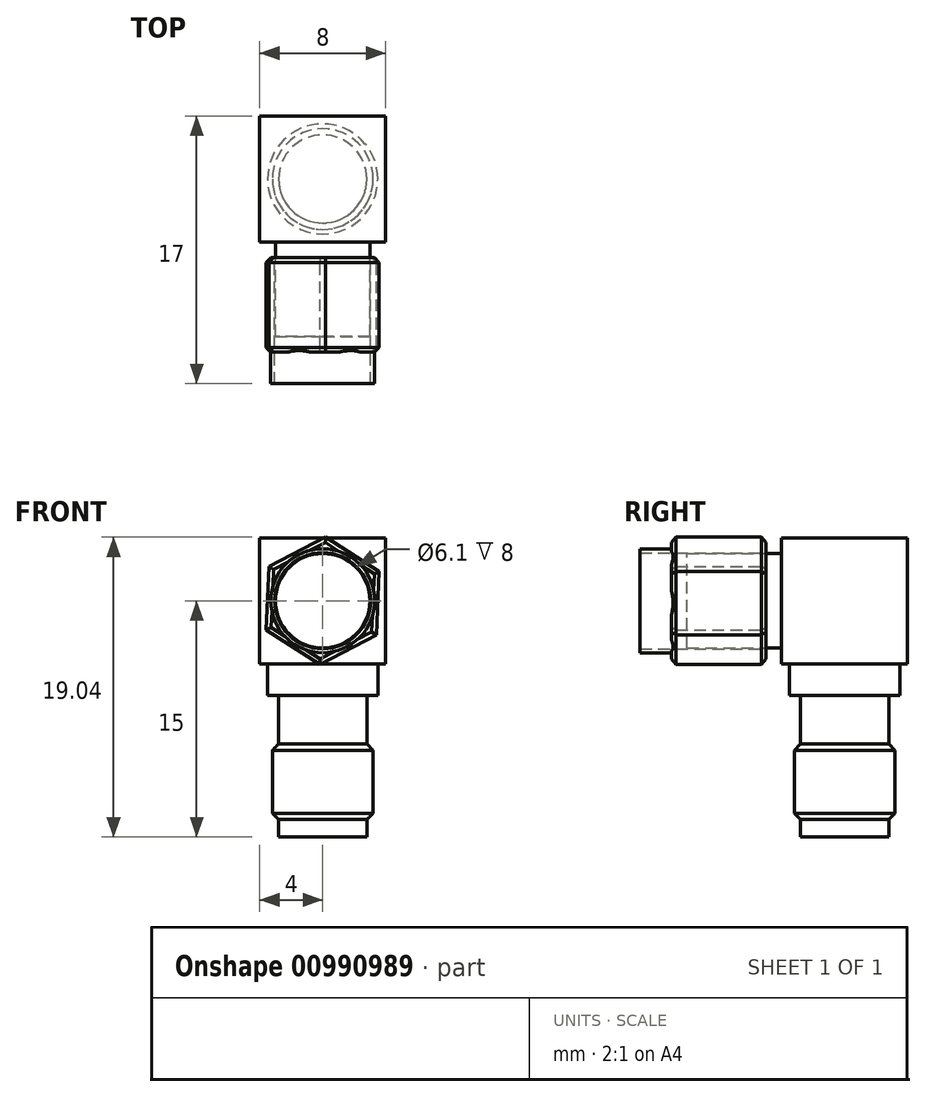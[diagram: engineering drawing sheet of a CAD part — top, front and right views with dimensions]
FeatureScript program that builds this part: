
annotation { "Feature Type Name" : "Feature", "Feature Type Description" : "" }
export const myFeature = defineFeature(function(context is Context, id is Id, definition is map)
    precondition{}
    {
        {
            var Q0;
            Q0=qCreatedBy(makeId("Top.planeOp"),FACE);
            var sketch = newSketch(context, id + "F0", { "sketchPlane" : qUnion([Q0])});
            skLineSegment(sketch, "E0.bottom", {"start": v(4, 4) * mm, "end": v(-4, 4) * mm});
            skLineSegment(sketch, "E0.top", {"start": v(4, -4) * mm, "end": v(-4, -4) * mm});
            skLineSegment(sketch, "E0.left", {"start": v(4, 4) * mm, "end": v(4, -4) * mm});
            skLineSegment(sketch, "E0.right", {"start": v(-4, 4) * mm, "end": v(-4, -4) * mm});
            skPoint(sketch, "E0.middle", {"position": v(0, 0) * mm});
            skSolve(sketch);
        }
        {
            var Q0;
            Q0=qSketchRegion(id+"F0",true);
            extrude(context, id + "F1", {"entities" : qUnion([Q0]), "depth" : 8 * mm, "offsetDistance" : 25 * mm});
        }
        {
            var Q0;
            Q0=makeQuery(id+"F1.opExtrude","CAP_FACE",FACE,{"disambiguationData":[OSD([sQuery(id+"F0.wireOp",EDGE,"E0.bottom"),sQuery(id+"F0.wireOp",EDGE,"E0.top"),sQuery(id+"F0.wireOp",EDGE,"E0.left"),sQuery(id+"F0.wireOp",EDGE,"E0.right")])],"isStart":true});
            var sketch = newSketch(context, id + "F2", { "sketchPlane" : qUnion([Q0])});
            skCircle(sketch, "E1", {"center": v(0, 0) * mm, "radius": 3.75 * mm});
            skSolve(sketch);
        }
        {
            var Q0;
            Q0=qCreatedBy(makeId("Right.planeOp"),FACE);
            var sketch = newSketch(context, id + "F3", { "sketchPlane" : qUnion([Q0])});
            skLineSegment(sketch, "E2", {"start": v(0, 0) * mm, "end": v(3.5, 0) * mm});
            skLineSegment(sketch, "E3", {"start": v(3.5, 0) * mm, "end": v(3.5, -2) * mm});
            skLineSegment(sketch, "E4", {"start": v(3.5, -2) * mm, "end": v(2.8, -2) * mm});
            skLineSegment(sketch, "E5", {"start": v(2.8, -2) * mm, "end": v(2.8, -5) * mm});
            skLineSegment(sketch, "E6", {"start": v(2.8, -5) * mm, "end": v(3.2, -5) * mm});
            skLineSegment(sketch, "E7", {"start": v(3.2, -5) * mm, "end": v(3.2, -10) * mm});
            skLineSegment(sketch, "E8", {"start": v(0, -11) * mm, "end": v(0, 0) * mm});
            skLineSegment(sketch, "E9", {"start": v(3.2, -10) * mm, "end": v(2.8, -10) * mm});
            skLineSegment(sketch, "E10", {"start": v(2.8, -10) * mm, "end": v(2.8, -11) * mm});
            skLineSegment(sketch, "E11", {"start": v(2.8, -11) * mm, "end": v(0, -11) * mm});
            skSolve(sketch);
        }
        {
            var Q0;
            Q0=makeQuery(id+"F3.imprint","IMPRINT",FACE,{"disambiguationData":[TD([[makeQuery(id+"F3.imprint","IMPRINT",EDGE,{"derivedFrom":sQuery(id+"F3.wireOp",EDGE,"E2")}),-1.0]])]});
            var Q1;
            Q1=sQuery(id+"F3.wireOp",EDGE,"E8");
            revolve(context, id + "F4", {"operationType" : NewBodyOperationType.ADD, "surfaceOperationType" : NewSurfaceOperationType.NEW, "entities" : qUnion([Q0]), "axis" : qUnion([Q1]), "revolveType" : RevolveType.FULL});
        }
        {
            var Q0;
            Q0=makeQuery(id+"F4.opRevolve","SWEPT_EDGE",EDGE,{"disambiguationData":[OSD([sQuery(id+"F3.wireOp",EDGE,"E7"),sQuery(id+"F3.wireOp",EDGE,"E9")])]});
            var Q1;
            Q1=makeQuery(id+"F4.opRevolve","SWEPT_EDGE",EDGE,{"disambiguationData":[OSD([sQuery(id+"F3.wireOp",EDGE,"E6"),sQuery(id+"F3.wireOp",EDGE,"E7")])]});
            chamfer(context, id + "F5", {"entities" : qUnion([Q0, Q1]), "width" : .5 * mm, "tangentPropagation" : true});
        }
        {
            var Q0;
            Q0=makeQuery(id+"F1.opExtrude","SWEPT_FACE",FACE,{"disambiguationData":[OSD([sQuery(id+"F0.wireOp",EDGE,"E0.top")])]});
            var sketch = newSketch(context, id + "F6", { "sketchPlane" : qUnion([Q0])});
            skCircle(sketch, "E12", {"center": v(0, 4) * mm, "radius": 3 * mm});
            skPoint(sketch, "E12.centerSnap0", {"position": v(-4, 4) * mm});
            skSolve(sketch);
        }
        {
            var Q0;
            Q0=qSketchRegion(id+"F6",true);
            var Q1;
            Q1=qConstructionFilter(qBodyType(qCreatedBy(id+"F6",EDGE),BodyType.WIRE),ConstructionObject.NO);
            extrude(context, id + "F7", {"entities" : qUnion([Q0]), "operationType" : NewBodyOperationType.ADD, "surfaceEntities" : qUnion([Q1]), "depth" : 6 * mm, "offsetDistance" : 25 * mm});
        }
        {
            var Q0;
            Q0=makeQuery(id+"F1.opExtrude","SWEPT_FACE",FACE,{"disambiguationData":[OSD([sQuery(id+"F0.wireOp",EDGE,"E0.top")])]});
            cPlane(context, id + "F8", {"entities" : qUnion([Q0]), "cplaneType" : CPlaneType.OFFSET, "offset" : 1 * mm, "width" : 150 * mm, "height" : 150 * mm});
        }
        {
            var Q0;
            Q0=qCreatedBy(id+"F8.planeOp",FACE);
            var sketch = newSketch(context, id + "F9", { "sketchPlane" : qUnion([Q0])});
            skCircle(sketch, "E13", {"center": v(0, 4) * mm, "radius": 3.05 * mm});
            skCircle(sketch, "E14.cCircle", {"center": v(0, 4) * mm, "radius": 3.5 * mm, "construction": true});
            skLineSegment(sketch, "E14.0", {"start": v(-0.18, -0.04) * mm, "end": v(-3.59, 2.14) * mm});
            skLineSegment(sketch, "E14.1", {"start": v(-3.59, 2.14) * mm, "end": v(-3.4, 6.17) * mm});
            skLineSegment(sketch, "E14.2", {"start": v(-3.4, 6.17) * mm, "end": v(0.18, 8.04) * mm});
            skLineSegment(sketch, "E14.3", {"start": v(0.18, 8.04) * mm, "end": v(3.59, 5.86) * mm});
            skLineSegment(sketch, "E14.4", {"start": v(3.59, 5.86) * mm, "end": v(3.4, 1.83) * mm});
            skLineSegment(sketch, "E14.5", {"start": v(3.4, 1.83) * mm, "end": v(-0.18, -0.04) * mm});
            skPoint(sketch, "E14.0.midPoint", {"position": v(-1.88, 1.05) * mm});
            skSolve(sketch);
        }
        {
            var Q0;
            Q0=qSketchRegion(id+"F9",true);
            extrude(context, id + "F10", {"entities" : qUnion([Q0]), "depth" : 8 * mm, "offsetDistance" : 25 * mm});
        }
        {
            var Q0;
            Q0=makeQuery(id+"F10.opExtrude","CAP_FACE",FACE,{"disambiguationData":[OSD([sQuery(id+"F9.wireOp",EDGE,"E13"),sQuery(id+"F9.wireOp",EDGE,"E14.0"),sQuery(id+"F9.wireOp",EDGE,"E14.1"),sQuery(id+"F9.wireOp",EDGE,"E14.2"),sQuery(id+"F9.wireOp",EDGE,"E14.3"),sQuery(id+"F9.wireOp",EDGE,"E14.4"),sQuery(id+"F9.wireOp",EDGE,"E14.5")])],"isStart":false});
            var sketch = newSketch(context, id + "F11", { "sketchPlane" : qUnion([Q0])});
            skCircle(sketch, "E15", {"center": v(0, 4) * mm, "radius": 3.3 * mm});
            skCircle(sketch, "E16", {"center": v(0, 4) * mm, "radius": 4.05 * mm});
            skSolve(sketch);
        }
        {
            var Q0;
            Q0=qSketchRegion(id+"F11",true);
            extrude(context, id + "F12", {"entities" : qUnion([Q0]), "operationType" : NewBodyOperationType.REMOVE, "oppositeDirection" : true, "depth" : 2 * mm, "offsetDistance" : 25 * mm});
        }
        {
            var Q0;
            Q0=makeQuery(id+"F12.boolean.opBoolean","INTERSECT",EDGE,{"derivedFrom":[makeQuery(id+"F10.opExtrude","SWEPT_FACE",FACE,{"disambiguationData":[OSD([sQuery(id+"F9.wireOp",EDGE,"E14.5")])]}),makeQuery(id+"F12.opExtrude","CAP_FACE",FACE,{"disambiguationData":[OSD([sQuery(id+"F11.wireOp",EDGE,"E15"),sQuery(id+"F11.wireOp",EDGE,"E16")])],"isStart":false})]});
            var Q1;
            Q1=makeQuery(id+"F12.boolean.opBoolean","INTERSECT",EDGE,{"derivedFrom":[makeQuery(id+"F10.opExtrude","SWEPT_FACE",FACE,{"disambiguationData":[OSD([sQuery(id+"F9.wireOp",EDGE,"E14.0")])]}),makeQuery(id+"F12.opExtrude","CAP_FACE",FACE,{"disambiguationData":[OSD([sQuery(id+"F11.wireOp",EDGE,"E15"),sQuery(id+"F11.wireOp",EDGE,"E16")])],"isStart":false})]});
            var Q2;
            Q2=makeQuery(id+"F12.boolean.opBoolean","INTERSECT",EDGE,{"derivedFrom":[makeQuery(id+"F10.opExtrude","SWEPT_FACE",FACE,{"disambiguationData":[OSD([sQuery(id+"F9.wireOp",EDGE,"E14.1")])]}),makeQuery(id+"F12.opExtrude","CAP_FACE",FACE,{"disambiguationData":[OSD([sQuery(id+"F11.wireOp",EDGE,"E15"),sQuery(id+"F11.wireOp",EDGE,"E16")])],"isStart":false})]});
            var Q3;
            Q3=makeQuery(id+"F10.opExtrude","CAP_EDGE",EDGE,{"disambiguationData":[OSD([sQuery(id+"F9.wireOp",EDGE,"E14.4")])],"isStart":true});
            var Q4;
            Q4=makeQuery(id+"F12.boolean.opBoolean","INTERSECT",EDGE,{"derivedFrom":[makeQuery(id+"F10.opExtrude","SWEPT_FACE",FACE,{"disambiguationData":[OSD([sQuery(id+"F9.wireOp",EDGE,"E14.4")])]}),makeQuery(id+"F12.opExtrude","CAP_FACE",FACE,{"disambiguationData":[OSD([sQuery(id+"F11.wireOp",EDGE,"E15"),sQuery(id+"F11.wireOp",EDGE,"E16")])],"isStart":false})]});
            var Q5;
            Q5=makeQuery(id+"F12.boolean.opBoolean","INTERSECT",EDGE,{"derivedFrom":[makeQuery(id+"F10.opExtrude","SWEPT_FACE",FACE,{"disambiguationData":[OSD([sQuery(id+"F9.wireOp",EDGE,"E14.3")])]}),makeQuery(id+"F12.opExtrude","CAP_FACE",FACE,{"disambiguationData":[OSD([sQuery(id+"F11.wireOp",EDGE,"E15"),sQuery(id+"F11.wireOp",EDGE,"E16")])],"isStart":false})]});
            var Q6;
            Q6=makeQuery(id+"F12.boolean.opBoolean","INTERSECT",EDGE,{"derivedFrom":[makeQuery(id+"F10.opExtrude","SWEPT_FACE",FACE,{"disambiguationData":[OSD([sQuery(id+"F9.wireOp",EDGE,"E14.2")])]}),makeQuery(id+"F12.opExtrude","CAP_FACE",FACE,{"disambiguationData":[OSD([sQuery(id+"F11.wireOp",EDGE,"E15"),sQuery(id+"F11.wireOp",EDGE,"E16")])],"isStart":false})]});
            var Q7;
            Q7=makeQuery(id+"F10.opExtrude","CAP_EDGE",EDGE,{"disambiguationData":[OSD([sQuery(id+"F9.wireOp",EDGE,"E14.2")])],"isStart":true});
            var Q8;
            Q8=makeQuery(id+"F10.opExtrude","CAP_EDGE",EDGE,{"disambiguationData":[OSD([sQuery(id+"F9.wireOp",EDGE,"E14.3")])],"isStart":true});
            var Q9;
            Q9=makeQuery(id+"F10.opExtrude","CAP_EDGE",EDGE,{"disambiguationData":[OSD([sQuery(id+"F9.wireOp",EDGE,"E14.5")])],"isStart":true});
            var Q10;
            Q10=makeQuery(id+"F10.opExtrude","CAP_EDGE",EDGE,{"disambiguationData":[OSD([sQuery(id+"F9.wireOp",EDGE,"E14.0")])],"isStart":true});
            var Q11;
            Q11=makeQuery(id+"F10.opExtrude","CAP_EDGE",EDGE,{"disambiguationData":[OSD([sQuery(id+"F9.wireOp",EDGE,"E14.1")])],"isStart":true});
            chamfer(context, id + "F13", {"entities" : qUnion([Q0, Q1, Q2, Q3, Q4, Q5, Q6, Q7, Q8, Q9, Q10, Q11]), "width" : .3 * mm, "tangentPropagation" : true});
        }
    });
